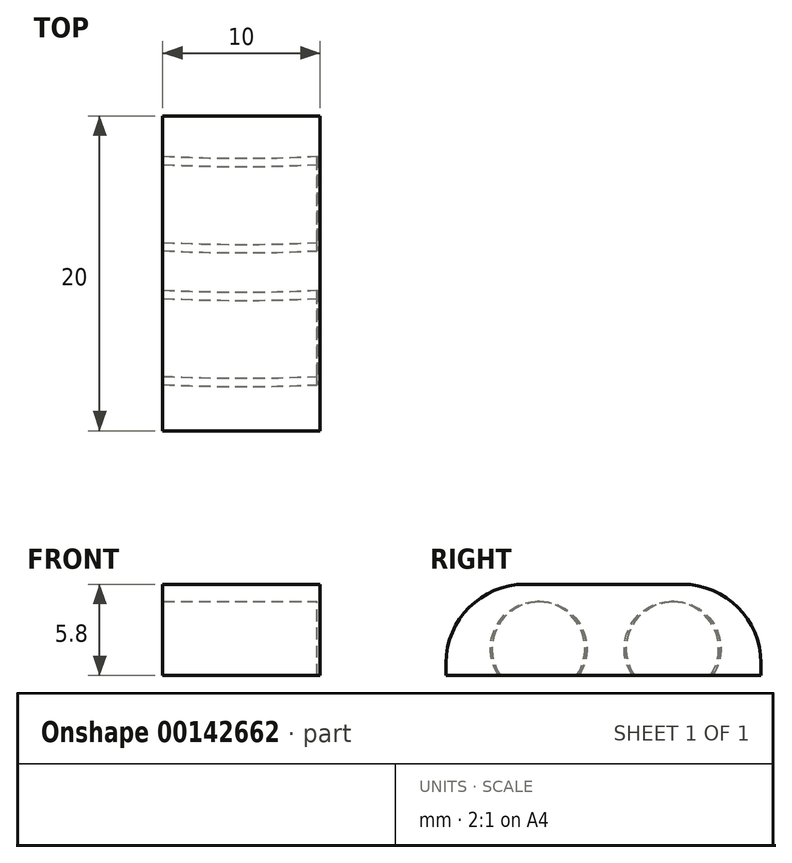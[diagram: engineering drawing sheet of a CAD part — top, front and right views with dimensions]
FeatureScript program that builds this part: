
annotation { "Feature Type Name" : "Feature", "Feature Type Description" : "" }
export const myFeature = defineFeature(function(context is Context, id is Id, definition is map)
    precondition{}
    {
        {
            var Q0;
            Q0=qCreatedBy(makeId("Front.planeOp"),FACE);
            var sketch = newSketch(context, id + "F0", { "sketchPlane" : qUnion([Q0])});
            skCircle(sketch, "E0", {"center": v(-91.5, 0) * mm, "radius": 3 * mm});
            skSolve(sketch);
        }
        {
            var Q0;
            Q0=qCreatedBy(makeId("Top.planeOp"),FACE);
            var sketch = newSketch(context, id + "F1", { "sketchPlane" : qUnion([Q0])});
            skPoint(sketch, "E1.0", {"position": v(-91.5, 0) * mm});
            skCircle(sketch, "E2", {"center": v(0, 0) * mm, "radius": 91.5 * mm});
            skSolve(sketch);
        }
        {
            var Q0;
            Q0=qCreatedBy(makeId("Front.planeOp"),FACE);
            var sketch = newSketch(context, id + "F2", { "sketchPlane" : qUnion([Q0])});
            skCircle(sketch, "E3", {"center": v(-100, 0) * mm, "radius": 3 * mm});
            skSolve(sketch);
        }
        {
            var Q0;
            Q0=qCreatedBy(makeId("Top.planeOp"),FACE);
            var sketch = newSketch(context, id + "F3", { "sketchPlane" : qUnion([Q0])});
            skPoint(sketch, "E4.0", {"position": v(-100, 0) * mm});
            skCircle(sketch, "E5", {"center": v(0, 0) * mm, "radius": 100 * mm, "construction": true});
            skSolve(sketch);
        }
        {
            var Q0;
            Q0=qCreatedBy(makeId("Top.planeOp"),FACE);
            cPlane(context, id + "F4", {"entities" : qUnion([Q0]), "cplaneType" : CPlaneType.OFFSET, "offset" : ((3.4 / 2) + 2.4) * mm, "width" : 150 * mm, "height" : 150 * mm});
        }
        {
            var Q0;
            Q0=qCreatedBy(id+"F4.planeOp",FACE);
            var sketch = newSketch(context, id + "F5", { "sketchPlane" : qUnion([Q0])});
            skLineSegment(sketch, "E6.bottom", {"start": v(5, -105.81) * mm, "end": v(-5, -105.81) * mm});
            skLineSegment(sketch, "E6.top", {"start": v(5, -85.81) * mm, "end": v(-5, -85.81) * mm});
            skLineSegment(sketch, "E6.left", {"start": v(5, -105.81) * mm, "end": v(5, -85.81) * mm});
            skLineSegment(sketch, "E6.right", {"start": v(-5, -105.81) * mm, "end": v(-5, -85.81) * mm});
            skPoint(sketch, "E6.middle", {"position": v(0, -95.81) * mm});
            skSolve(sketch);
        }
        {
            var Q0;
            Q0 = qSketchRegion(id + "F5", true);
            extrude(context, id + "F6", {"entities" : qUnion([Q0]), "oppositeDirection" : true, "depth" : (3.4 + 2.4) * mm});
        }
        {
            var Q0;
            Q0 = qSketchRegion(id + "F0", true);
            var Q1;
            Q1=sQuery(id+"F1.wireOp",EDGE,"E2");
            revolve(context, id + "F7", {"operationType" : NewBodyOperationType.REMOVE, "entities" : qUnion([Q0]), "axis" : qUnion([Q1]), "revolveType" : RevolveType.FULL});
        }
        {
            var Q0;
            Q0 = qSketchRegion(id + "F2", true);
            var Q1;
            Q1=sQuery(id+"F3.wireOp",EDGE,"E5");
            revolve(context, id + "F8", {"operationType" : NewBodyOperationType.REMOVE, "entities" : qUnion([Q0]), "axis" : qUnion([Q1]), "revolveType" : RevolveType.FULL});
        }
        {
            var Q0;
            Q0=makeQuery(id+"F6.opExtrude","CAP_EDGE",EDGE,{"disambiguationData":[OSD([sQuery(id+"F5.wireOp",EDGE,"E6.bottom")])],"isStart":true});
            var Q1;
            Q1=makeQuery(id+"F6.opExtrude","CAP_EDGE",EDGE,{"disambiguationData":[OSD([sQuery(id+"F5.wireOp",EDGE,"E6.top")])],"isStart":true});
            fillet(context, id + "F9", {"entities" : qUnion([Q0, Q1]), "radius" : 5 * mm, "tangentPropagation" : true, "allowEdgeOverflow" : false});
        }
        {
            var Q0;
            Q0=makeQuery(id+"F6.opExtrude","SWEPT_FACE",FACE,{"disambiguationData":[OSD([sQuery(id+"F5.wireOp",EDGE,"E6.left")])]});
            var sketch = newSketch(context, id + "F10", { "sketchPlane" : qUnion([Q0])});
            skPoint(sketch, "E7", {"position": v(-85.81, -1.7) * mm});
            skPoint(sketch, "E8", {"position": v(-105.81, -1.7) * mm});
            skLineSegment(sketch, "E9.0", {"start": v(-100.81, 4.1) * mm, "end": v(-90.81, 4.1) * mm});
            skArc(sketch, "E10.0", {"start": v(-85.81, -0.9) * mm, "mid": v(-87.28, 2.64) * mm, "end": v(-90.81, 4.1) * mm});
            skLineSegment(sketch, "E11.0", {"start": v(-85.81, -1.7) * mm, "end": v(-85.81, -0.9) * mm});
            skArc(sketch, "E12.0", {"start": v(-100.81, 4.1) * mm, "mid": v(-104.35, 2.64) * mm, "end": v(-105.81, -0.9) * mm});
            skLineSegment(sketch, "E13.0", {"start": v(-105.81, -1.7) * mm, "end": v(-105.81, -0.9) * mm});
            skLineSegment(sketch, "E14", {"start": v(-105.81, -1.7) * mm, "end": v(-85.81, -1.7) * mm});
            skSolve(sketch);
        }
        {
            var Q0;
            Q0 = qSketchRegion(id + "F10", true);
            extrude(context, id + "F11", {"entities" : qUnion([Q0]), "operationType" : NewBodyOperationType.ADD, "oppositeDirection" : true, "depth" : 0.2 * mm});
        }
    });
